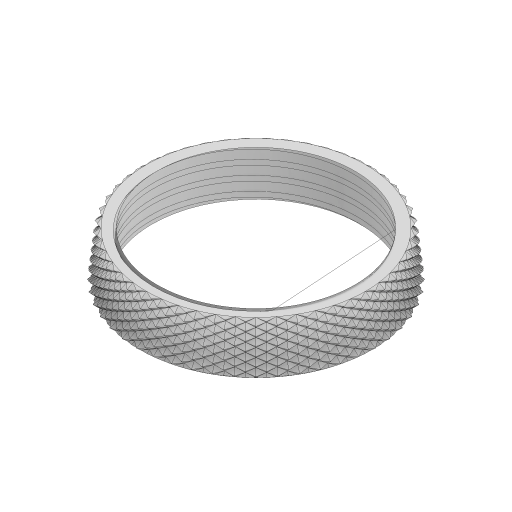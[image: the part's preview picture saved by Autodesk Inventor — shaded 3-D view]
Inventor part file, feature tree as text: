
AUTODESK INVENTOR PART (.ipt)
format: ipt  version: 2023 (Build 270158000, 158)  size: 9,723,904 bytes
history: native  units: mm
features: sketch x5, helix x3, draft x2, extrude x1, pattern_circular x1, mirror x1, revolve x1, projected_geometry x1
ambient origin geometry x8: Origin, YZ Plane, XZ Plane, XY Plane, X Axis, Y Axis, Z Axis, Center Point
bodies: Solid1 (feature_tree)
feature tree (15):
  extrude  "Extrusion1"  Depth=6.52mm TaperAngle=0.0deg
  draft  "FaceDraft1"
  sketch  "Sketch2"  dims[d7=2.0mm d8=9.0mm d9=10.0mm d10=1.047198mm d11=90.0deg d12=90.0deg d13=0.0mm d14=0.0mm d15=2.0mm d16=3.0mm d17=10.0mm d18=-1.047198mm d19=90.0deg d20=90.0deg d21=0.0mm d22=0.0mm d23=2.8mm d91=1.047198mm d109=1.308997mm]
  sketch  "Sketch4"  dims[d112=2.0mm d113=6.52mm d114=1.25mm d115=1.047198mm]
  helix  "Coil1"  [1 undecoded]
  helix  "Coil2"  [1 undecoded]
  draft  "FaceDraft2"
  helix  "Coil10"  [1 undecoded]
  pattern_circular  "Circular Pattern5"  Count=48 Angle=360.0deg
  mirror  "Mirror1"
  revolve  "Revolution2"  [1 undecoded]
  sketch  "Sketch1"  dims[d0=26.5mm d2=6.52mm d3=0.0mm d4=1.047198mm]
  sketch  "Sketch13"  dims[d116=90.0deg d117=90.0deg d118=0.0mm d119=0.0mm d122=480.0mm d123=360.0deg]
  sketch  "Sketch14"  dims[d127=60.0deg d128=14.703424mm d129=360.0deg d130=8.726646mm]
  projected_geometry  "Project Cut Edges1"
note: 4 required parameter values undecoded (feature->parameter linkage not recoverable at this tier; creation-order binding heuristic only, values carry confidence <= 0.55)